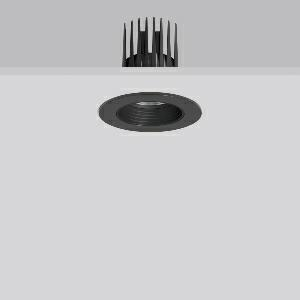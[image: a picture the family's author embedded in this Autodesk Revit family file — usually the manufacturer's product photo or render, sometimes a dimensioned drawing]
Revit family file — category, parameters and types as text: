
# Revit family: heledon_mini_e_901745_003_3_76_7d66
name_source: partatom
category: Lighting Fixtures
units: mm (PartAtom-declared; Revit-internal decimal feet)

## family parameters
Cut with Voids When Loaded = No
Host = Face
Light Source = No
Part Type = Normal
Room Calculation Point = No
Round Connector Dimension = Use Diameter
Shared = No

## types (1)
- HELEDON mini E (1 x LED Modul 935, 2000 lm, 3500)
    Apparent Load = 20 VA
    Approval mark = CE
    CIE Flux Codes = 98 100 100 100 100
    Color Rendering = 92
    Color Temperature = 3500
    Default Elevation = 1800 mm
    Description = Series: HELEDON mini
Round recessed downlight. Housing: die-cast aluminium, powder-coated. Black plastic ring and recessed LED to prevent glare from the side. Optical assembly with lens made of plastic (polycarbonate) for the best homogeneous light distribution - can be changed without tools. Best colour rendering index Ra>90. Suitable for Recessed ceiling mounting. Installation without tools thanks to spring fastening system. Including separate LED converter with connecting cable 600 mm.High quality converter without flickering and stroboscopic effect. Through-wiring box (5 pole) available as accessory. The following accessories can be mounted without use of tools: interchangeable lenses, decorative glasses, honeycomb louvre, clear and frosted diffusers, white interchangeable plastic ring. 
Colour: deep black, matt (RAL 9005)
Diameter: 124 mm
Height: 3 mm
Cut-out diameter: 114 mm
Recess height: 170 mm
Luminaire: recess height: 120 mm
Lamp: LED
Socket: without socket
Colour temperature: 3500K
Colour rendering index (CRI): 92
System power: 20 W
Rated luminous flux: 2000 lm
Luminous efficiency: 100 lm/W
Control gear: Converter, dimmable, DALI
Protection class: II
Type of protection: IP 20
    Height = 0 mm  [stored 0 ft]
    Lamp = 1 x LED Modul 935
    Lamp Light Flux = 2000 lm
    Lamp count = 1
    Length = 124 mm  [stored 0.406824 ft]
    Lifetime = 50000 h
    Luminous efficacy = 100 lm/W
    Manufacturer = RZB
    ModVariant = No
    Model = 901745.003.3.76
    Mounting Place = Ceiling
    Mounting Type = Recessed
    Number of Poles = 1
    OnlyDefault = Yes
    Power Factor = 1
    Product Name = HELEDON mini E
    Product group = Recessed downlights
    ProductGroupID = 402
    Protection Class = Protection class II
    Protection Degree = IP 20
    RLX_Detail_Level = 1
    RLX_Emergency_Light_Flux = 0 lm
    RLX_Emergency_Type = 0
    RLX_Emergency_Type_DB = No
    RlxData = <blob elided: 125449 chars, md5=132c9999>
    Socket = socket
    Standby Power = 0 W
    System Light Flux = 2000 lm
    System Power = 20 W
    Type Comments = Product without accessories
    Type Image = 901656.003.jpg
    URL = http://relux.com
    VarID = ---
    Voltage = 230 V
    Voltage Range = 220-240 V
    Weight = 0.00 kg
    Width = 0 mm  [stored 0 ft]

note: [stored X ft] marks values corroborated as IEEE doubles in the binary element streams (Revit-internal decimal feet)

## geometry (parser evidence)
native form markers: Blend x4, Sweep x11
no freeform markers — native parametric forms only
